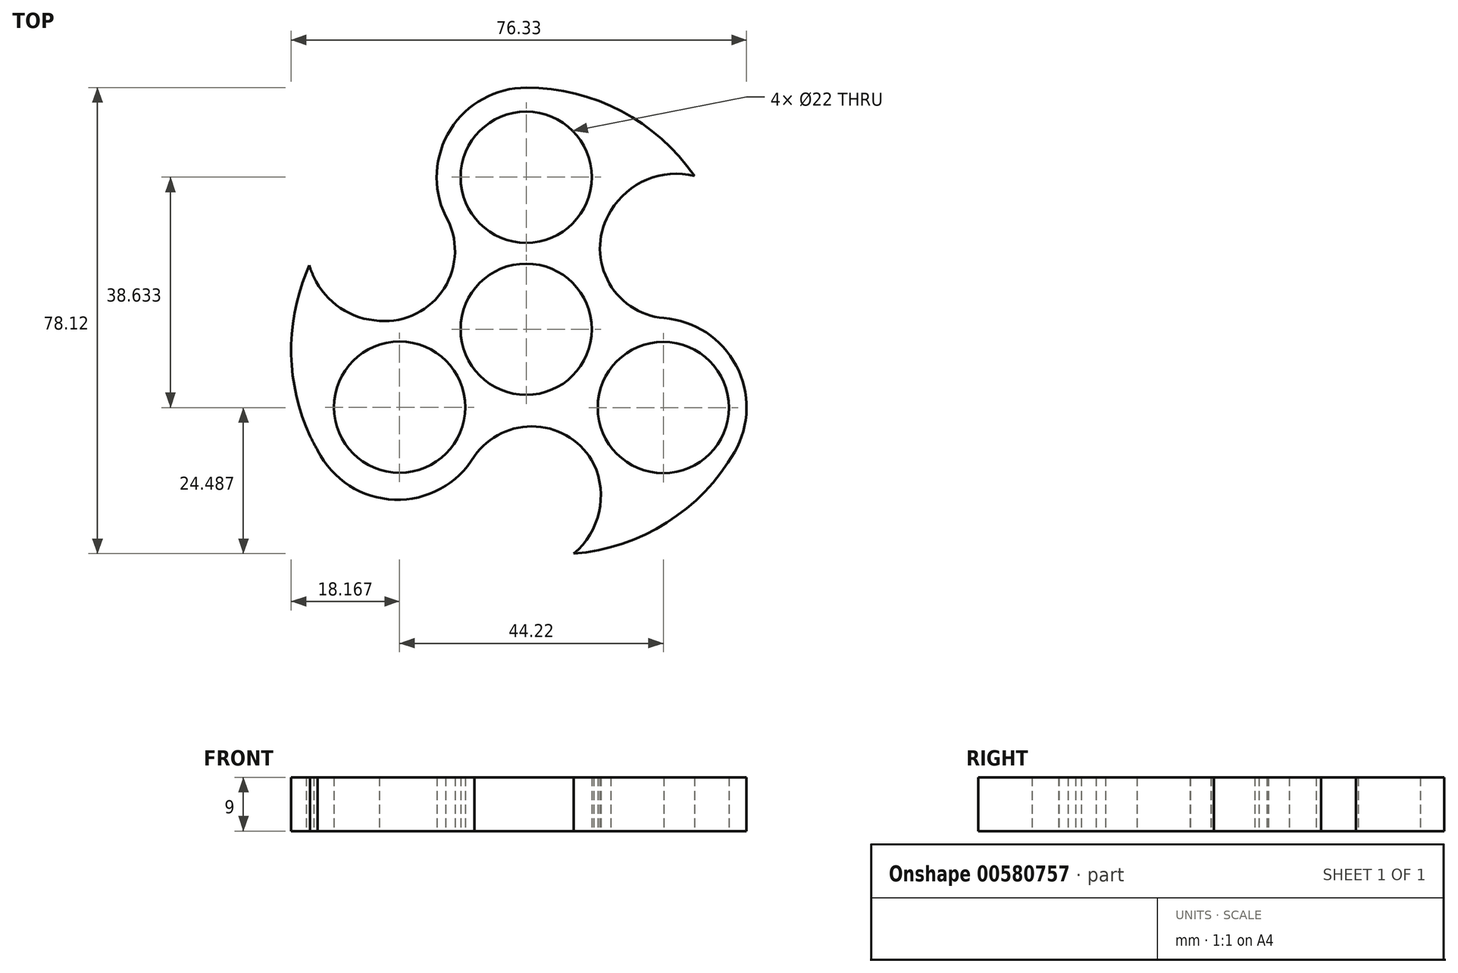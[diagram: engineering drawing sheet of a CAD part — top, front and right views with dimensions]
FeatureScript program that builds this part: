
annotation { "Feature Type Name" : "Feature", "Feature Type Description" : "" }
export const myFeature = defineFeature(function(context is Context, id is Id, definition is map)
    precondition{}
    {
        {
            var Q0;
            Q0=qCreatedBy(makeId("Top.planeOp"),FACE);
            var sketch = newSketch(context, id + "F0", { "sketchPlane" : qUnion([Q0])});
            skCircle(sketch, "E0.0", {"center": v(0, 0) * mm, "radius": 11 * mm});
            skCircle(sketch, "E1.0", {"center": v(-21.23, -13.07) * mm, "radius": 11 * mm});
            skArc(sketch, "E2.0", {"start": v(-36.23, -17.89) * mm, "mid": v(-39.39, -4.28) * mm, "end": v(-36.85, 9.46) * mm});
            skArc(sketch, "E3.0", {"start": v(-35.6, 8.76) * mm, "mid": v(-31.13, 3.55) * mm, "end": v(-24.6, 1.42) * mm});
            skArc(sketch, "E4.0", {"start": v(-35.6, 8.76) * mm, "mid": v(-36.02, 9.74) * mm, "end": v(-36.36, 10.75) * mm});
            skArc(sketch, "E5.0", {"start": v(-24.6, 1.42) * mm, "mid": v(-13.75, 6.87) * mm, "end": v(-13.52, 19) * mm});
            skArc(sketch, "E6.0", {"start": v(-13.52, 19) * mm, "mid": v(-12.7, 33.49) * mm, "end": v(0, 40.5) * mm});
            skArc(sketch, "E7.0", {"start": v(0, 40.5) * mm, "mid": v(15.93, 36.57) * mm, "end": v(28.21, 25.69) * mm});
            skArc(sketch, "E8.0", {"start": v(28.21, 25.69) * mm, "mid": v(20.24, 25.1) * mm, "end": v(14.19, 19.86) * mm});
            skArc(sketch, "E9.0", {"start": v(14.19, 19.86) * mm, "mid": v(13.58, 8.37) * mm, "end": v(23.07, 1.87) * mm});
            skArc(sketch, "E10.0", {"start": v(23.07, 1.87) * mm, "mid": v(35.2, -6.09) * mm, "end": v(34.92, -20.59) * mm});
            skArc(sketch, "E11.0", {"start": v(34.92, -20.59) * mm, "mid": v(23.55, -32.42) * mm, "end": v(7.99, -37.62) * mm});
            skArc(sketch, "E12.0", {"start": v(7.99, -37.62) * mm, "mid": v(12.2, -30.66) * mm, "end": v(11.34, -22.58) * mm});
            skArc(sketch, "E13.0", {"start": v(11.34, -22.58) * mm, "mid": v(1.7, -16.3) * mm, "end": v(-8.68, -21.28) * mm});
            skArc(sketch, "E14.0", {"start": v(-8.68, -21.28) * mm, "mid": v(-22.1, -28.57) * mm, "end": v(-34.96, -20.32) * mm});
            skArc(sketch, "E15.0", {"start": v(-34.96, -20.32) * mm, "mid": v(-35.62, -19.12) * mm, "end": v(-36.23, -17.89) * mm});
            skCircle(sketch, "E16.0", {"center": v(0, 25.5) * mm, "radius": 11 * mm});
            skCircle(sketch, "E17.0", {"center": v(22.99, -13.13) * mm, "radius": 11 * mm});
            skLineSegment(sketch, "E18", {"start": v(-36.85, 9.46) * mm, "end": v(-36.36, 10.75) * mm});
            skSolve(sketch);
        }
        {
            var Q0;
            Q0 = qSketchRegion(id + "F0", true);
            extrude(context, id + "F1", {"entities" : qUnion([Q0]), "depth" : 9 * mm, "offsetDistance" : 25 * mm});
        }
    });
